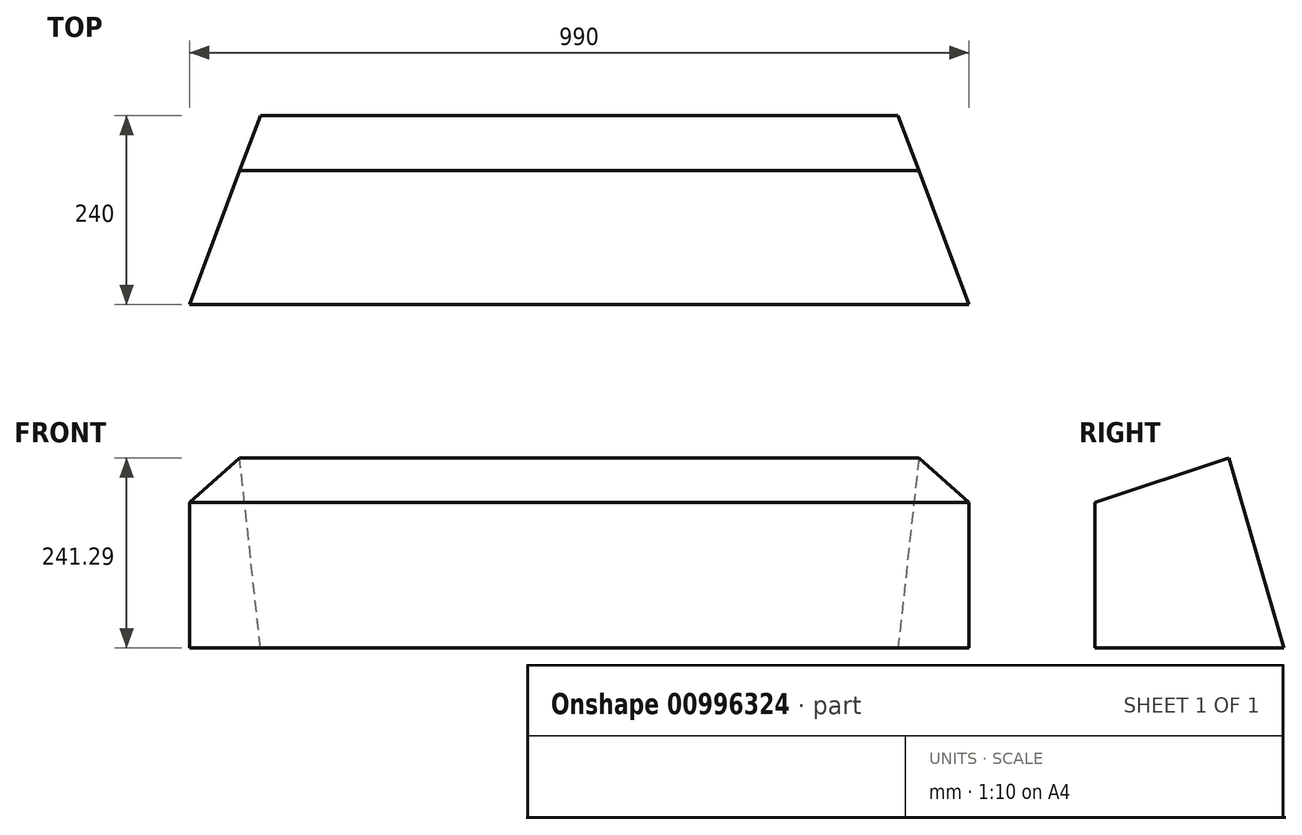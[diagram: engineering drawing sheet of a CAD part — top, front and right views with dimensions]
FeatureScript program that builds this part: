
annotation { "Feature Type Name" : "Feature", "Feature Type Description" : "" }
export const myFeature = defineFeature(function(context is Context, id is Id, definition is map)
    precondition{}
    {
        {
            var Q0;
            Q0=qCreatedBy(makeId("Top.planeOp"),FACE);
            var sketch = newSketch(context, id + "F0", { "sketchPlane" : qUnion([Q0])});
            skLineSegment(sketch, "E0", {"start": v(-495, 0) * mm, "end": v(495, 0) * mm});
            skLineSegment(sketch, "E1", {"start": v(495, 0) * mm, "end": v(405, 240) * mm});
            skLineSegment(sketch, "E2", {"start": v(405, 240) * mm, "end": v(-405, 240) * mm});
            skLineSegment(sketch, "E3", {"start": v(-405, 240) * mm, "end": v(-495, 0) * mm});
            skSolve(sketch);
        }
        {
            var Q0;
            Q0 = qSketchRegion(id + "F0", true);
            extrude(context, id + "F1", {"entities" : qUnion([Q0]), "depth" : 270 * mm, "offsetDistance" : 25 * mm});
        }
        {
            var Q0;
            Q0=makeQuery(id+"F1.opExtrude","SWEPT_FACE",FACE,{"disambiguationData":[OSD([sQuery(id+"F0.wireOp",EDGE,"E1")])]});
            var sketch = newSketch(context, id + "F2", { "sketchPlane" : qUnion([Q0])});
            skLineSegment(sketch, "E4", {"start": v(-173.8, 0) * mm, "end": v(-173.8, 185) * mm});
            skLineSegment(sketch, "E5", {"start": v(-173.8, 185) * mm, "end": v(7.66, 241.3) * mm});
            skLineSegment(sketch, "E6", {"start": v(7.66, 241.3) * mm, "end": v(82.51, 0) * mm});
            skLineSegment(sketch, "E7", {"start": v(-173.8, 0) * mm, "end": v(82.51, 0) * mm});
            skSolve(sketch);
        }
        {
            var Q0;
            Q0=qCreatedBy(makeId("Right.planeOp"),FACE);
            var sketch = newSketch(context, id + "F3", { "sketchPlane" : qUnion([Q0])});
            skLineSegment(sketch, "E8.0", {"start": v(0, 185) * mm, "end": v(169.91, 241.3) * mm});
            skLineSegment(sketch, "E8.1", {"start": v(169.91, 241.3) * mm, "end": v(240, 0) * mm});
            skLineSegment(sketch, "E8.2", {"start": v(0, 0) * mm, "end": v(240, 0) * mm});
            skLineSegment(sketch, "E8.3", {"start": v(0, 0) * mm, "end": v(0, 185) * mm});
            skSolve(sketch);
        }
        {
            var Q0;
            Q0 = qSketchRegion(id + "F3", true);
            extrude(context, id + "F4", {"entities" : qUnion([Q0]), "operationType" : NewBodyOperationType.INTERSECT, "depth" : 1000 * mm, "offsetDistance" : 25 * mm, "symmetric" : true});
        }
    });
